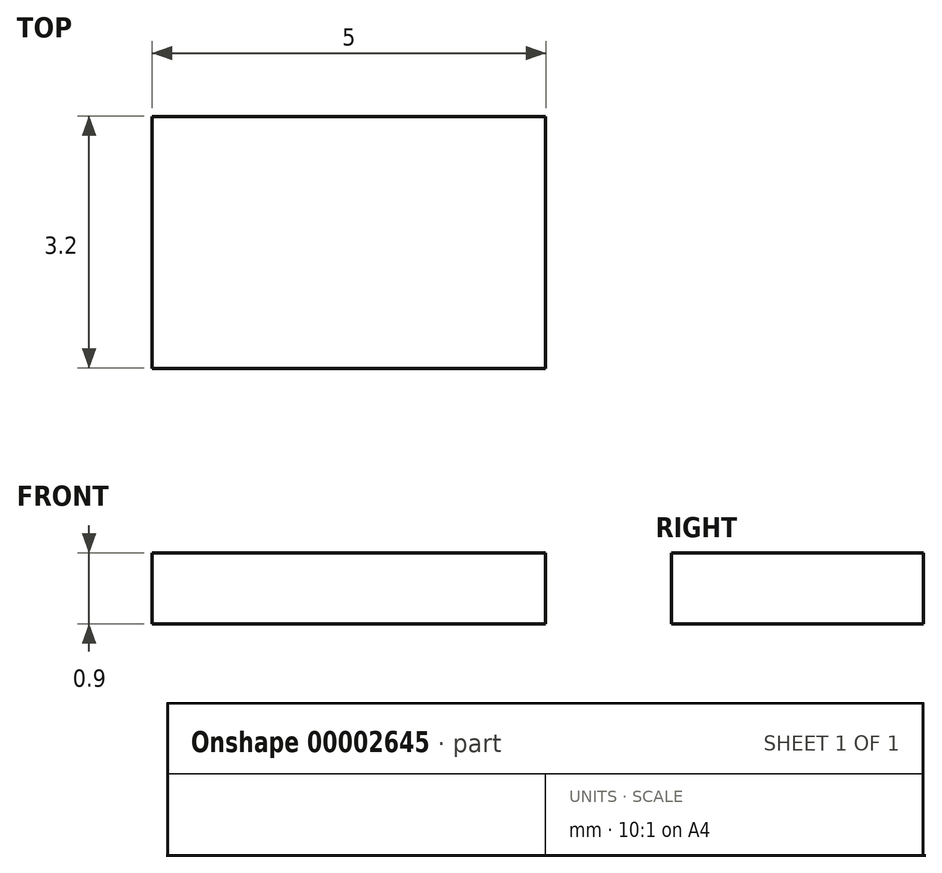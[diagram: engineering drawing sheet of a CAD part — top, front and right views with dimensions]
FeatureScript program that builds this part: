
annotation { "Feature Type Name" : "Feature", "Feature Type Description" : "" }
export const myFeature = defineFeature(function(context is Context, id is Id, definition is map)
    precondition{}
    {
        {
            var Q0;
            Q0=qCreatedBy(makeId("Top.planeOp"),FACE);
            var sketch = newSketch(context, id + "F0", { "sketchPlane" : qUnion([Q0])});
            skLineSegment(sketch, "E0.bottom", {"start": v(-0.51, 3.13) * mm, "end": v(4.49, 3.13) * mm});
            skLineSegment(sketch, "E0.top", {"start": v(-0.51, -0.07) * mm, "end": v(4.49, -0.07) * mm});
            skLineSegment(sketch, "E0.left", {"start": v(-0.51, 3.13) * mm, "end": v(-0.51, -0.07) * mm});
            skLineSegment(sketch, "E0.right", {"start": v(4.49, 3.13) * mm, "end": v(4.49, -0.07) * mm});
            skSolve(sketch);
        }
        {
            var Q0;
            Q0=makeQuery(id+"F0.imprint","IMPRINT",FACE,{"disambiguationData":[TD([[makeQuery(id+"F0.imprint","IMPRINT",EDGE,{"derivedFrom":sQuery(id+"F0.wireOp",EDGE,"E0.bottom")}),-1.0]])]});
            extrude(context, id + "F1", {"entities" : qUnion([Q0]), "depth" : .9 * mm});
        }
    });
